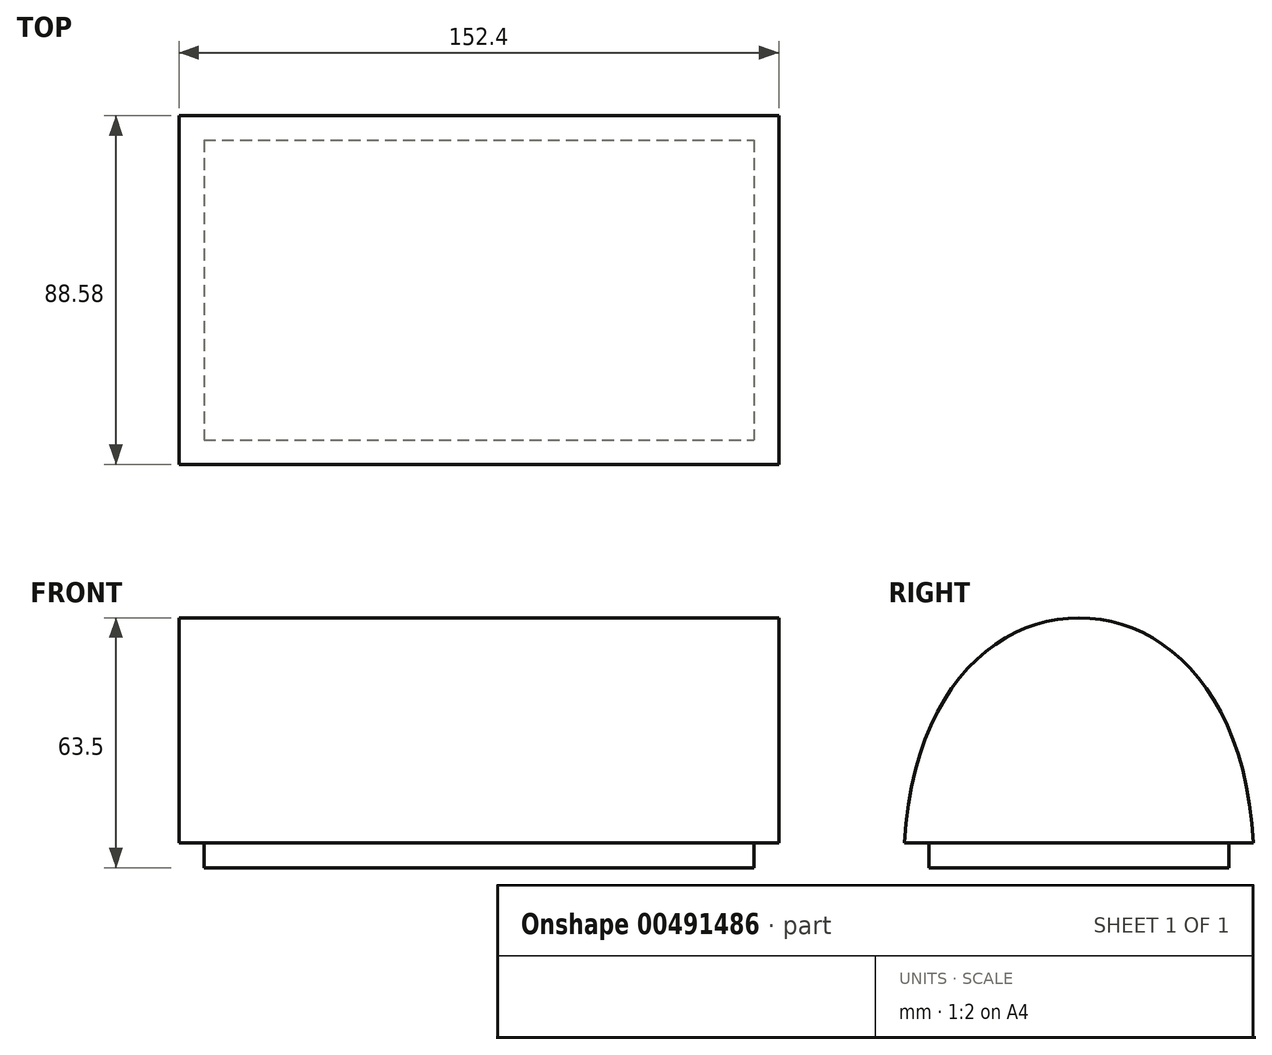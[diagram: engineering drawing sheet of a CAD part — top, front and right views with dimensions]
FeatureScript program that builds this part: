
annotation { "Feature Type Name" : "Feature", "Feature Type Description" : "" }
export const myFeature = defineFeature(function(context is Context, id is Id, definition is map)
    precondition{}
    {
        {
            var Q0;
            Q0=qCreatedBy(makeId("Right.planeOp"),FACE);
            var sketch = newSketch(context, id + "F0", { "sketchPlane" : qUnion([Q0])});
            skLineSegment(sketch, "E0.bottom", {"start": v(44.45, -63.5) * mm, "end": v(-44.45, -63.5) * mm});
            skLineSegment(sketch, "E0.top", {"start": v(44.45, 63.5) * mm, "end": v(-44.45, 63.5) * mm});
            skLineSegment(sketch, "E0.left", {"start": v(44.45, -63.5) * mm, "end": v(44.45, 63.5) * mm});
            skLineSegment(sketch, "E0.right", {"start": v(-44.45, -63.5) * mm, "end": v(-44.45, 63.5) * mm});
            skPoint(sketch, "E0.middle", {"position": v(0, 0) * mm});
            skPoint(sketch, "E1", {"position": v(0, 63.5) * mm});
            skFitSpline(sketch, "E2", {"points": [v(-44.45, 0) * mm, v(0, 63.5) * mm, v(44.45, 0) * mm], "startDerivative": vector(0, 260.17) * mm, "endDerivative": vector(0, -260.17) * mm});
            skLineSegment(sketch, "E3", {"start": v(-44.45, 0) * mm, "end": v(44.45, 0) * mm});
            skSolve(sketch);
        }
        {
            var Q0;
            {var subQ0=sQuery(id+"F0.wireOp",EDGE,"E3");Q0=makeQuery(id+"F0.imprint","IMPRINT",FACE,{"disambiguationData":[TD([[makeQuery(id+"F0.imprint","IMPRINT",EDGE,{"derivedFrom":subQ0}),1.0]])]});}
            extrude(context, id + "F1", {"entities" : qUnion([Q0]), "depth" : 76.2 * mm});
        }
        {
            var Q0;
            Q0=makeQuery(id+"F1.opExtrude","CAP_FACE",FACE,{"disambiguationData":[OSD([sQuery(id+"F0.wireOp",EDGE,"E2"),sQuery(id+"F0.wireOp",EDGE,"E3")])],"isStart":true});
            extrude(context, id + "F2", {"entities" : qUnion([Q0]), "operationType" : NewBodyOperationType.ADD, "depth" : 76.2 * mm});
        }
        {
            var Q0;
            {var subQ0=sQuery(id+"F0.wireOp",EDGE,"E3");Q0=makeQuery(id+"F2.boolean.opBoolean","MERGE",FACE,{"derivedFrom":[makeQuery(id+"F1.opExtrude","SWEPT_FACE",FACE,{"disambiguationData":[OSD([subQ0])]}),makeQuery(id+"F2.opExtrude","SWEPT_FACE",FACE,{"disambiguationData":[OSD([subQ0])]})]});}
            var sketch = newSketch(context, id + "F3", { "sketchPlane" : qUnion([Q0])});
            skPoint(sketch, "E4", {"position": v(-69.85, -38.1) * mm});
            skPoint(sketch, "E5", {"position": v(69.85, 38.1) * mm});
            skLineSegment(sketch, "E6.bottom", {"start": v(-69.85, -38.1) * mm, "end": v(69.85, -38.1) * mm});
            skLineSegment(sketch, "E6.top", {"start": v(-69.85, 38.1) * mm, "end": v(69.85, 38.1) * mm});
            skLineSegment(sketch, "E6.left", {"start": v(-69.85, -38.1) * mm, "end": v(-69.85, 38.1) * mm});
            skLineSegment(sketch, "E6.right", {"start": v(69.85, -38.1) * mm, "end": v(69.85, 38.1) * mm});
            skSolve(sketch);
        }
        {
            var Q0;
            Q0=makeQuery(id+"F3.imprint","IMPRINT",FACE,{"disambiguationData":[TD([[makeQuery(id+"F3.imprint","IMPRINT",EDGE,{"derivedFrom":sQuery(id+"F3.wireOp",EDGE,"E6.bottom")}),-1.0]])]});
            extrude(context, id + "F4", {"entities" : qUnion([Q0]), "operationType" : NewBodyOperationType.REMOVE, "oppositeDirection" : true, "depth" : 6.35 * mm});
        }
    });
